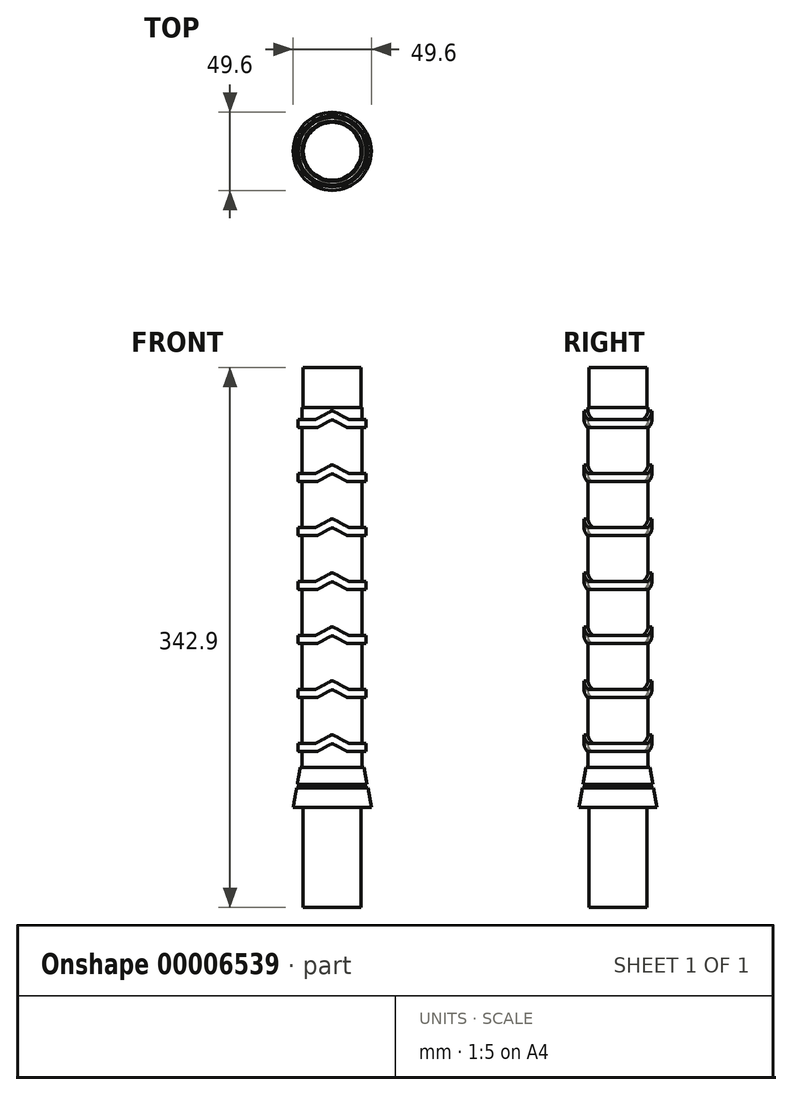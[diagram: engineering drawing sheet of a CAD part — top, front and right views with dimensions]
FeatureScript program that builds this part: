
annotation { "Feature Type Name" : "Feature", "Feature Type Description" : "" }
export const myFeature = defineFeature(function(context is Context, id is Id, definition is map)
    precondition{}
    {
        {
            var Q0;
            Q0=qCreatedBy(makeId("Top.planeOp"),FACE);
            var sketch = newSketch(context, id + "F0", { "sketchPlane" : qUnion([Q0])});
            skCircle(sketch, "E0", {"center": v(0, 0) * mm, "radius": 18.41 * mm});
            skSolve(sketch);
        }
        {
            var Q0;
            Q0=makeQuery(id+"F0.imprint","IMPRINT",FACE,{"disambiguationData":[TD([[makeQuery(id+"F0.imprint","IMPRINT",EDGE,{"derivedFrom":sQuery(id+"F0.wireOp",EDGE,"E0")}),1.0]])]});
            extrude(context, id + "F1", {"entities" : qUnion([Q0]), "depth" : 63.5 * mm});
        }
        {
            var Q0;
            Q0=makeQuery(id+"F1.opExtrude","CAP_FACE",FACE,{"disambiguationData":[OSD([sQuery(id+"F0.wireOp",EDGE,"E0")])],"isStart":false});
            var sketch = newSketch(context, id + "F2", { "sketchPlane" : qUnion([Q0])});
            skCircle(sketch, "E1", {"center": v(0, 0) * mm, "radius": 25.4 * mm});
            skSolve(sketch);
        }
        {
            var Q0;
            Q0=makeQuery(id+"F2.imprint","IMPRINT",FACE,{"disambiguationData":[TD([[makeQuery(id+"F2.imprint","IMPRINT",EDGE,{"derivedFrom":makeQuery(id+"F1.opExtrude","CAP_EDGE",EDGE,{"disambiguationData":[OSD([sQuery(id+"F0.wireOp",EDGE,"E0")])],"isStart":false})}),1.0]])]});
            var Q1;
            Q1=makeQuery(id+"F2.imprint","IMPRINT",FACE,{"disambiguationData":[TD([[makeQuery(id+"F2.imprint","IMPRINT",EDGE,{"derivedFrom":sQuery(id+"F2.wireOp",EDGE,"E1")}),1.0]])]});
            extrude(context, id + "F3", {"entities" : qUnion([Q0, Q1]), "operationType" : NewBodyOperationType.ADD, "depth" : 25.4 * mm});
        }
        {
            var Q0;
            Q0=makeQuery(id+"F3.opExtrude","CAP_FACE",FACE,{"disambiguationData":[OSD([sQuery(id+"F2.wireOp",EDGE,"E1")])],"isStart":false});
            chamfer(context, id + "F4", {"entities" : qUnion([Q0]), "chamferType" : ChamferType.OFFSET_ANGLE, "width" : 5.08 * mm, "oppositeDirection" : false, "angle" : 80 * degree, "tangentPropagation" : true});
        }
        {
            var Q0;
            Q0=makeQuery(id+"F3.opExtrude","CAP_FACE",FACE,{"disambiguationData":[OSD([sQuery(id+"F2.wireOp",EDGE,"E1")])],"isStart":false});
            var sketch = newSketch(context, id + "F5", { "sketchPlane" : qUnion([Q0])});
            skCircle(sketch, "E2", {"center": v(0, 0) * mm, "radius": 19.05 * mm});
            skSolve(sketch);
        }
        {
            var Q0;
            Q0=makeQuery(id+"F5.imprint","IMPRINT",FACE,{"disambiguationData":[TD([[makeQuery(id+"F5.imprint","IMPRINT",EDGE,{"derivedFrom":sQuery(id+"F5.wireOp",EDGE,"E2")}),1.0]])]});
            extrude(context, id + "F6", {"entities" : qUnion([Q0]), "operationType" : NewBodyOperationType.ADD, "depth" : 254 * mm});
        }
        {
            var Q0;
            Q0=makeQuery(id+"F6.opExtrude","CAP_FACE",FACE,{"disambiguationData":[OSD([sQuery(id+"F5.wireOp",EDGE,"E2")])],"isStart":false});
            var sketch = newSketch(context, id + "F7", { "sketchPlane" : qUnion([Q0])});
            skCircle(sketch, "E3", {"center": v(0, 0) * mm, "radius": 34.67 * mm});
            skCircle(sketch, "E4", {"center": v(0, 0) * mm, "radius": 18.41 * mm});
            skSolve(sketch);
        }
        {
            var Q0;
            Q0=qCreatedBy(makeId("Front.planeOp"),FACE);
            var sketch = newSketch(context, id + "F8", { "sketchPlane" : qUnion([Q0])});
            skLineSegment(sketch, "E5", {"start": v(21.53, 75.72) * mm, "end": v(24.03, 75.72) * mm});
            skLineSegment(sketch, "E6", {"start": v(24.03, 75.72) * mm, "end": v(23.44, 77.96) * mm});
            skLineSegment(sketch, "E7", {"start": v(21.53, 75.72) * mm, "end": v(21.13, 77.96) * mm});
            skLineSegment(sketch, "E8", {"start": v(21.13, 77.96) * mm, "end": v(23.44, 77.96) * mm});
            skSolve(sketch);
        }
        {
            var Q0;
            Q0=makeQuery(id+"F8.imprint","IMPRINT",FACE,{"disambiguationData":[TD([[makeQuery(id+"F8.imprint","IMPRINT",EDGE,{"derivedFrom":sQuery(id+"F8.wireOp",EDGE,"E5")}),1.0]])]});
            var Q1;
            Q1=makeQuery(id+"F4.opChamfer","BLEND_FACE",FACE,{"disambiguationData":[OSD([sQuery(id+"F2.wireOp",EDGE,"E1")])]});
            revolve(context, id + "F9", {"operationType" : NewBodyOperationType.REMOVE, "entities" : qUnion([Q0]), "axis" : qUnion([Q1]), "revolveType" : RevolveType.FULL, "oppositeDirection" : true});
        }
        {
            var Q0;
            Q0=qCreatedBy(makeId("Front.planeOp"),FACE);
            var sketch = newSketch(context, id + "F10", { "sketchPlane" : qUnion([Q0])});
            skLineSegment(sketch, "E9.0", {"start": v(-20.32, 88.9) * mm, "end": v(20.32, 88.9) * mm});
            skLineSegment(sketch, "E10.bottom", {"start": v(-70.85, 99.06) * mm, "end": v(-9.89, 99.06) * mm});
            skLineSegment(sketch, "E10.top", {"start": v(-70.85, 104.14) * mm, "end": v(-11.11, 104.14) * mm});
            skLineSegment(sketch, "E10.left", {"start": v(-70.85, 99.06) * mm, "end": v(-70.85, 104.14) * mm});
            skLineSegment(sketch, "E10.right", {"start": v(67.66, 99.06) * mm, "end": v(67.66, 104.14) * mm});
            skLineSegment(sketch, "E11", {"start": v(-8.66, 99.37) * mm, "end": v(-1.22, 103.47) * mm});
            skLineSegment(sketch, "E12.0.MirrorCS", {"start": v(8.66, 99.37) * mm, "end": v(1.22, 103.47) * mm});
            skLineSegment(sketch, "E13.0", {"start": v(9.89, 104.45) * mm, "end": v(1.22, 109.22) * mm});
            skLineSegment(sketch, "E13.1", {"start": v(-9.89, 104.45) * mm, "end": v(-1.22, 109.22) * mm});
            skLineSegment(sketch, "E14.trimOffspring", {"start": v(11.11, 104.14) * mm, "end": v(67.66, 104.14) * mm});
            skPoint(sketch, "E15.start.orphan", {"position": v(0, 99.06) * mm});
            skLineSegment(sketch, "E16.trimOffspring", {"start": v(9.89, 99.06) * mm, "end": v(67.66, 99.06) * mm});
            skPoint(sketch, "E17.visualSharp", {"position": v(0, 109.9) * mm});
            skArc(sketch, "E17.filletArc", {"start": v(1.22, 109.22) * mm, "mid": v(0, 109.54) * mm, "end": v(-1.22, 109.22) * mm});
            skPoint(sketch, "E18.visualSharp", {"position": v(0, 104.14) * mm});
            skArc(sketch, "E18.filletArc", {"start": v(1.22, 103.47) * mm, "mid": v(0, 103.78) * mm, "end": v(-1.22, 103.47) * mm});
            skPoint(sketch, "E19.visualSharp", {"position": v(9.23, 99.06) * mm});
            skArc(sketch, "E19.filletArc", {"start": v(8.66, 99.37) * mm, "mid": v(9.25, 99.14) * mm, "end": v(9.89, 99.06) * mm});
            skPoint(sketch, "E20.visualSharp", {"position": v(10.46, 104.14) * mm});
            skArc(sketch, "E20.filletArc", {"start": v(9.89, 104.45) * mm, "mid": v(10.48, 104.22) * mm, "end": v(11.11, 104.14) * mm});
            skPoint(sketch, "E21.visualSharp", {"position": v(-9.23, 99.06) * mm});
            skArc(sketch, "E21.filletArc", {"start": v(-9.89, 99.06) * mm, "mid": v(-9.25, 99.14) * mm, "end": v(-8.66, 99.37) * mm});
            skPoint(sketch, "E22.visualSharp", {"position": v(-10.46, 104.14) * mm});
            skArc(sketch, "E22.filletArc", {"start": v(-11.11, 104.14) * mm, "mid": v(-10.48, 104.22) * mm, "end": v(-9.89, 104.45) * mm});
            skLineSegment(sketch, "E23.0.1.0", {"start": v(-70.85, 138.43) * mm, "end": v(-11.11, 138.43) * mm});
            skLineSegment(sketch, "E23.0.1.1", {"start": v(-70.85, 133.35) * mm, "end": v(-9.89, 133.35) * mm});
            skLineSegment(sketch, "E23.0.1.2", {"start": v(-9.89, 138.74) * mm, "end": v(-1.22, 143.51) * mm});
            skLineSegment(sketch, "E23.0.1.3", {"start": v(-8.66, 133.66) * mm, "end": v(-1.22, 137.76) * mm});
            skArc(sketch, "E23.0.1.4", {"start": v(-11.11, 138.43) * mm, "mid": v(-10.48, 138.5) * mm, "end": v(-9.89, 138.74) * mm});
            skArc(sketch, "E23.0.1.5", {"start": v(-9.89, 133.35) * mm, "mid": v(-9.25, 133.43) * mm, "end": v(-8.66, 133.66) * mm});
            skArc(sketch, "E23.0.1.6", {"start": v(1.22, 143.51) * mm, "mid": v(0, 143.83) * mm, "end": v(-1.22, 143.51) * mm});
            skArc(sketch, "E23.0.1.7", {"start": v(1.22, 137.76) * mm, "mid": v(0, 138.07) * mm, "end": v(-1.22, 137.76) * mm});
            skLineSegment(sketch, "E23.0.1.8", {"start": v(8.66, 133.66) * mm, "end": v(1.22, 137.76) * mm});
            skLineSegment(sketch, "E23.0.1.9", {"start": v(9.89, 138.74) * mm, "end": v(1.22, 143.51) * mm});
            skLineSegment(sketch, "E23.0.1.10", {"start": v(9.89, 133.35) * mm, "end": v(67.66, 133.35) * mm});
            skLineSegment(sketch, "E23.0.1.11", {"start": v(11.11, 138.43) * mm, "end": v(67.66, 138.43) * mm});
            skLineSegment(sketch, "E23.0.1.12", {"start": v(-70.85, 133.35) * mm, "end": v(-70.85, 138.43) * mm});
            skLineSegment(sketch, "E23.0.1.13", {"start": v(67.66, 133.35) * mm, "end": v(67.66, 138.43) * mm});
            skArc(sketch, "E23.0.1.14", {"start": v(8.66, 133.66) * mm, "mid": v(9.25, 133.43) * mm, "end": v(9.89, 133.35) * mm});
            skArc(sketch, "E23.0.1.15", {"start": v(9.89, 138.74) * mm, "mid": v(10.48, 138.5) * mm, "end": v(11.11, 138.43) * mm});
            skLineSegment(sketch, "E23.0.2.0", {"start": v(-70.85, 172.72) * mm, "end": v(-11.11, 172.72) * mm});
            skLineSegment(sketch, "E23.0.2.1", {"start": v(-70.85, 167.64) * mm, "end": v(-9.89, 167.64) * mm});
            skLineSegment(sketch, "E23.0.2.2", {"start": v(-9.89, 173.03) * mm, "end": v(-1.22, 177.8) * mm});
            skLineSegment(sketch, "E23.0.2.3", {"start": v(-8.66, 167.95) * mm, "end": v(-1.22, 172.05) * mm});
            skArc(sketch, "E23.0.2.4", {"start": v(-11.11, 172.72) * mm, "mid": v(-10.48, 172.8) * mm, "end": v(-9.89, 173.03) * mm});
            skArc(sketch, "E23.0.2.5", {"start": v(-9.89, 167.64) * mm, "mid": v(-9.25, 167.72) * mm, "end": v(-8.66, 167.95) * mm});
            skArc(sketch, "E23.0.2.6", {"start": v(1.22, 177.8) * mm, "mid": v(0, 178.12) * mm, "end": v(-1.22, 177.8) * mm});
            skArc(sketch, "E23.0.2.7", {"start": v(1.22, 172.05) * mm, "mid": v(0, 172.36) * mm, "end": v(-1.22, 172.05) * mm});
            skLineSegment(sketch, "E23.0.2.8", {"start": v(8.66, 167.95) * mm, "end": v(1.22, 172.05) * mm});
            skLineSegment(sketch, "E23.0.2.9", {"start": v(9.89, 173.03) * mm, "end": v(1.22, 177.8) * mm});
            skLineSegment(sketch, "E23.0.2.10", {"start": v(9.89, 167.64) * mm, "end": v(67.66, 167.64) * mm});
            skLineSegment(sketch, "E23.0.2.11", {"start": v(11.11, 172.72) * mm, "end": v(67.66, 172.72) * mm});
            skLineSegment(sketch, "E23.0.2.12", {"start": v(-70.85, 167.64) * mm, "end": v(-70.85, 172.72) * mm});
            skLineSegment(sketch, "E23.0.2.13", {"start": v(67.66, 167.64) * mm, "end": v(67.66, 172.72) * mm});
            skArc(sketch, "E23.0.2.14", {"start": v(8.66, 167.95) * mm, "mid": v(9.25, 167.72) * mm, "end": v(9.89, 167.64) * mm});
            skArc(sketch, "E23.0.2.15", {"start": v(9.89, 173.03) * mm, "mid": v(10.48, 172.8) * mm, "end": v(11.11, 172.72) * mm});
            skLineSegment(sketch, "E23.0.3.0", {"start": v(-70.85, 207.01) * mm, "end": v(-11.11, 207.01) * mm});
            skLineSegment(sketch, "E23.0.3.1", {"start": v(-70.85, 201.93) * mm, "end": v(-9.89, 201.93) * mm});
            skLineSegment(sketch, "E23.0.3.2", {"start": v(-9.89, 207.32) * mm, "end": v(-1.22, 212.1) * mm});
            skLineSegment(sketch, "E23.0.3.3", {"start": v(-8.66, 202.24) * mm, "end": v(-1.22, 206.34) * mm});
            skArc(sketch, "E23.0.3.4", {"start": v(-11.11, 207.01) * mm, "mid": v(-10.48, 207.09) * mm, "end": v(-9.89, 207.32) * mm});
            skArc(sketch, "E23.0.3.5", {"start": v(-9.89, 201.93) * mm, "mid": v(-9.25, 202) * mm, "end": v(-8.66, 202.24) * mm});
            skArc(sketch, "E23.0.3.6", {"start": v(1.22, 212.1) * mm, "mid": v(0, 212.4) * mm, "end": v(-1.22, 212.1) * mm});
            skArc(sketch, "E23.0.3.7", {"start": v(1.22, 206.34) * mm, "mid": v(0, 206.65) * mm, "end": v(-1.22, 206.34) * mm});
            skLineSegment(sketch, "E23.0.3.8", {"start": v(8.66, 202.24) * mm, "end": v(1.22, 206.34) * mm});
            skLineSegment(sketch, "E23.0.3.9", {"start": v(9.89, 207.32) * mm, "end": v(1.22, 212.1) * mm});
            skLineSegment(sketch, "E23.0.3.10", {"start": v(9.89, 201.93) * mm, "end": v(67.66, 201.93) * mm});
            skLineSegment(sketch, "E23.0.3.11", {"start": v(11.11, 207.01) * mm, "end": v(67.66, 207.01) * mm});
            skLineSegment(sketch, "E23.0.3.12", {"start": v(-70.85, 201.93) * mm, "end": v(-70.85, 207.01) * mm});
            skLineSegment(sketch, "E23.0.3.13", {"start": v(67.66, 201.93) * mm, "end": v(67.66, 207.01) * mm});
            skArc(sketch, "E23.0.3.14", {"start": v(8.66, 202.24) * mm, "mid": v(9.25, 202) * mm, "end": v(9.89, 201.93) * mm});
            skArc(sketch, "E23.0.3.15", {"start": v(9.89, 207.32) * mm, "mid": v(10.48, 207.09) * mm, "end": v(11.11, 207.01) * mm});
            skLineSegment(sketch, "E23.0.4.0", {"start": v(-70.85, 241.3) * mm, "end": v(-11.11, 241.3) * mm});
            skLineSegment(sketch, "E23.0.4.1", {"start": v(-70.85, 236.22) * mm, "end": v(-9.89, 236.22) * mm});
            skLineSegment(sketch, "E23.0.4.2", {"start": v(-9.89, 241.61) * mm, "end": v(-1.22, 246.38) * mm});
            skLineSegment(sketch, "E23.0.4.3", {"start": v(-8.66, 236.53) * mm, "end": v(-1.22, 240.63) * mm});
            skArc(sketch, "E23.0.4.4", {"start": v(-11.11, 241.3) * mm, "mid": v(-10.48, 241.38) * mm, "end": v(-9.89, 241.61) * mm});
            skArc(sketch, "E23.0.4.5", {"start": v(-9.89, 236.22) * mm, "mid": v(-9.25, 236.3) * mm, "end": v(-8.66, 236.53) * mm});
            skArc(sketch, "E23.0.4.6", {"start": v(1.22, 246.38) * mm, "mid": v(0, 246.7) * mm, "end": v(-1.22, 246.38) * mm});
            skArc(sketch, "E23.0.4.7", {"start": v(1.22, 240.63) * mm, "mid": v(0, 240.94) * mm, "end": v(-1.22, 240.63) * mm});
            skLineSegment(sketch, "E23.0.4.8", {"start": v(8.66, 236.53) * mm, "end": v(1.22, 240.63) * mm});
            skLineSegment(sketch, "E23.0.4.9", {"start": v(9.89, 241.61) * mm, "end": v(1.22, 246.38) * mm});
            skLineSegment(sketch, "E23.0.4.10", {"start": v(9.89, 236.22) * mm, "end": v(67.66, 236.22) * mm});
            skLineSegment(sketch, "E23.0.4.11", {"start": v(11.11, 241.3) * mm, "end": v(67.66, 241.3) * mm});
            skLineSegment(sketch, "E23.0.4.12", {"start": v(-70.85, 236.22) * mm, "end": v(-70.85, 241.3) * mm});
            skLineSegment(sketch, "E23.0.4.13", {"start": v(67.66, 236.22) * mm, "end": v(67.66, 241.3) * mm});
            skArc(sketch, "E23.0.4.14", {"start": v(8.66, 236.53) * mm, "mid": v(9.25, 236.3) * mm, "end": v(9.89, 236.22) * mm});
            skArc(sketch, "E23.0.4.15", {"start": v(9.89, 241.61) * mm, "mid": v(10.48, 241.38) * mm, "end": v(11.11, 241.3) * mm});
            skLineSegment(sketch, "E23.0.5.0", {"start": v(-70.85, 275.6) * mm, "end": v(-11.11, 275.6) * mm});
            skLineSegment(sketch, "E23.0.5.1", {"start": v(-70.85, 270.51) * mm, "end": v(-9.89, 270.51) * mm});
            skLineSegment(sketch, "E23.0.5.2", {"start": v(-9.89, 275.9) * mm, "end": v(-1.22, 280.67) * mm});
            skLineSegment(sketch, "E23.0.5.3", {"start": v(-8.66, 270.82) * mm, "end": v(-1.22, 274.92) * mm});
            skArc(sketch, "E23.0.5.4", {"start": v(-11.11, 275.6) * mm, "mid": v(-10.48, 275.67) * mm, "end": v(-9.89, 275.9) * mm});
            skArc(sketch, "E23.0.5.5", {"start": v(-9.89, 270.51) * mm, "mid": v(-9.25, 270.59) * mm, "end": v(-8.66, 270.82) * mm});
            skArc(sketch, "E23.0.5.6", {"start": v(1.22, 280.67) * mm, "mid": v(0, 280.99) * mm, "end": v(-1.22, 280.67) * mm});
            skArc(sketch, "E23.0.5.7", {"start": v(1.22, 274.92) * mm, "mid": v(0, 275.23) * mm, "end": v(-1.22, 274.92) * mm});
            skLineSegment(sketch, "E23.0.5.8", {"start": v(8.66, 270.82) * mm, "end": v(1.22, 274.92) * mm});
            skLineSegment(sketch, "E23.0.5.9", {"start": v(9.89, 275.9) * mm, "end": v(1.22, 280.67) * mm});
            skLineSegment(sketch, "E23.0.5.10", {"start": v(9.89, 270.51) * mm, "end": v(67.66, 270.51) * mm});
            skLineSegment(sketch, "E23.0.5.11", {"start": v(11.11, 275.6) * mm, "end": v(67.66, 275.6) * mm});
            skLineSegment(sketch, "E23.0.5.12", {"start": v(-70.85, 270.51) * mm, "end": v(-70.85, 275.6) * mm});
            skLineSegment(sketch, "E23.0.5.13", {"start": v(67.66, 270.51) * mm, "end": v(67.66, 275.6) * mm});
            skArc(sketch, "E23.0.5.14", {"start": v(8.66, 270.82) * mm, "mid": v(9.25, 270.59) * mm, "end": v(9.89, 270.51) * mm});
            skArc(sketch, "E23.0.5.15", {"start": v(9.89, 275.9) * mm, "mid": v(10.48, 275.67) * mm, "end": v(11.11, 275.6) * mm});
            skLineSegment(sketch, "E23.0.6.0", {"start": v(-70.85, 309.88) * mm, "end": v(-11.11, 309.88) * mm});
            skLineSegment(sketch, "E23.0.6.1", {"start": v(-70.85, 304.8) * mm, "end": v(-9.89, 304.8) * mm});
            skLineSegment(sketch, "E23.0.6.2", {"start": v(-9.89, 310.2) * mm, "end": v(-1.22, 314.96) * mm});
            skLineSegment(sketch, "E23.0.6.3", {"start": v(-8.66, 305.11) * mm, "end": v(-1.22, 309.2) * mm});
            skArc(sketch, "E23.0.6.4", {"start": v(-11.11, 309.88) * mm, "mid": v(-10.48, 309.96) * mm, "end": v(-9.89, 310.2) * mm});
            skArc(sketch, "E23.0.6.5", {"start": v(-9.89, 304.8) * mm, "mid": v(-9.25, 304.88) * mm, "end": v(-8.66, 305.11) * mm});
            skArc(sketch, "E23.0.6.6", {"start": v(1.22, 314.96) * mm, "mid": v(0, 315.28) * mm, "end": v(-1.22, 314.96) * mm});
            skArc(sketch, "E23.0.6.7", {"start": v(1.22, 309.2) * mm, "mid": v(0, 309.52) * mm, "end": v(-1.22, 309.2) * mm});
            skLineSegment(sketch, "E23.0.6.8", {"start": v(8.66, 305.11) * mm, "end": v(1.22, 309.2) * mm});
            skLineSegment(sketch, "E23.0.6.9", {"start": v(9.89, 310.2) * mm, "end": v(1.22, 314.96) * mm});
            skLineSegment(sketch, "E23.0.6.10", {"start": v(9.89, 304.8) * mm, "end": v(67.66, 304.8) * mm});
            skLineSegment(sketch, "E23.0.6.11", {"start": v(11.11, 309.88) * mm, "end": v(67.66, 309.88) * mm});
            skLineSegment(sketch, "E23.0.6.12", {"start": v(-70.85, 304.8) * mm, "end": v(-70.85, 309.88) * mm});
            skLineSegment(sketch, "E23.0.6.13", {"start": v(67.66, 304.8) * mm, "end": v(67.66, 309.88) * mm});
            skArc(sketch, "E23.0.6.14", {"start": v(8.66, 305.11) * mm, "mid": v(9.25, 304.88) * mm, "end": v(9.89, 304.8) * mm});
            skArc(sketch, "E23.0.6.15", {"start": v(9.89, 310.2) * mm, "mid": v(10.48, 309.96) * mm, "end": v(11.11, 309.88) * mm});
            skLineSegment(sketch, "E23.direction1", {"start": v(-70.85, 104.14) * mm, "end": v(-45.45, 104.14) * mm, "construction": true});
            skLineSegment(sketch, "E23.direction2", {"start": v(-70.85, 104.14) * mm, "end": v(-70.85, 138.43) * mm, "construction": true});
            skSolve(sketch);
        }
        {
            var Q0;
            Q0=makeQuery(id+"F10.imprint","IMPRINT",FACE,{"disambiguationData":[TD([[makeQuery(id+"F10.imprint","IMPRINT",EDGE,{"derivedFrom":sQuery(id+"F10.wireOp",EDGE,"E10.bottom")}),1.0]])]});
            var Q1;
            Q1=makeQuery(id+"F10.imprint","IMPRINT",FACE,{"disambiguationData":[TD([[makeQuery(id+"F10.imprint","IMPRINT",EDGE,{"derivedFrom":sQuery(id+"F10.wireOp",EDGE,"E23.0.1.0")}),-1.0]])]});
            var Q2;
            Q2=makeQuery(id+"F10.imprint","IMPRINT",FACE,{"disambiguationData":[TD([[makeQuery(id+"F10.imprint","IMPRINT",EDGE,{"derivedFrom":sQuery(id+"F10.wireOp",EDGE,"E23.0.2.0")}),-1.0]])]});
            var Q3;
            Q3=makeQuery(id+"F10.imprint","IMPRINT",FACE,{"disambiguationData":[TD([[makeQuery(id+"F10.imprint","IMPRINT",EDGE,{"derivedFrom":sQuery(id+"F10.wireOp",EDGE,"E23.0.3.0")}),-1.0]])]});
            var Q4;
            Q4=makeQuery(id+"F10.imprint","IMPRINT",FACE,{"disambiguationData":[TD([[makeQuery(id+"F10.imprint","IMPRINT",EDGE,{"derivedFrom":sQuery(id+"F10.wireOp",EDGE,"E23.0.4.0")}),-1.0]])]});
            var Q5;
            Q5=makeQuery(id+"F10.imprint","IMPRINT",FACE,{"disambiguationData":[TD([[makeQuery(id+"F10.imprint","IMPRINT",EDGE,{"derivedFrom":sQuery(id+"F10.wireOp",EDGE,"E23.0.5.0")}),-1.0]])]});
            var Q6;
            Q6=makeQuery(id+"F10.imprint","IMPRINT",FACE,{"disambiguationData":[TD([[makeQuery(id+"F10.imprint","IMPRINT",EDGE,{"derivedFrom":sQuery(id+"F10.wireOp",EDGE,"E23.0.6.0")}),-1.0]])]});
            extrude(context, id + "F11", {"entities" : qUnion([Q0, Q1, Q2, Q3, Q4, Q5, Q6]), "operationType" : NewBodyOperationType.ADD, "endBound" : BoundingType.SYMMETRIC, "depth" : 76.2 * mm});
        }
        {
            var Q0;
            Q0=makeQuery(id+"F3.opExtrude","CAP_FACE",FACE,{"disambiguationData":[OSD([sQuery(id+"F2.wireOp",EDGE,"E1")])],"isStart":false});
            var sketch = newSketch(context, id + "F12", { "sketchPlane" : qUnion([Q0])});
            skCircle(sketch, "E24", {"center": v(0, 0) * mm, "radius": 21.59 * mm});
            skCircle(sketch, "E25.0", {"center": v(0, 0) * mm, "radius": 19.05 * mm});
            skCircle(sketch, "E26", {"center": v(0, 0) * mm, "radius": 88.29 * mm});
            skSolve(sketch);
        }
        {
            var Q0;
            Q0=makeQuery(id+"F12.imprint","IMPRINT",FACE,{"disambiguationData":[TD([[makeQuery(id+"F12.imprint","IMPRINT",EDGE,{"derivedFrom":sQuery(id+"F12.wireOp",EDGE,"E24")}),-1.0]])]});
            extrude(context, id + "F13", {"entities" : qUnion([Q0]), "operationType" : NewBodyOperationType.REMOVE, "depth" : 254 * mm});
        }
        {
            var Q0;
            Q0=makeQuery(id+"F7.imprint","IMPRINT",FACE,{"disambiguationData":[TD([[makeQuery(id+"F7.imprint","IMPRINT",EDGE,{"derivedFrom":sQuery(id+"F7.wireOp",EDGE,"E4")}),-1.0]])]});
            var Q1;
            Q1=makeQuery(id+"F7.imprint","IMPRINT",FACE,{"disambiguationData":[TD([[makeQuery(id+"F7.imprint","IMPRINT",EDGE,{"derivedFrom":sQuery(id+"F7.wireOp",EDGE,"E3")}),1.0]])]});
            extrude(context, id + "F14", {"entities" : qUnion([Q0, Q1]), "operationType" : NewBodyOperationType.REMOVE, "oppositeDirection" : true, "depth" : 25.4 * mm});
        }
    });
